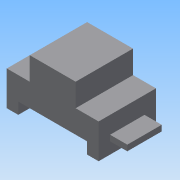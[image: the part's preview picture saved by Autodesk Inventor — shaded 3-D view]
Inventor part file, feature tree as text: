
AUTODESK INVENTOR PART (.ipt)
format: ipt  version: 2015 (Build 190159000, 159)  size: 96,768 bytes
history: native  units: in
note: dims shown in document units (in); Inventor stores cm internally (conversion verified against a paired STEP export)
features: sketch x4, extrude x2
ambient origin geometry x8: Origin, YZ Plane, XZ Plane, XY Plane, X Axis, Y Axis, Z Axis, Center Point
bodies: Solid1 (feature_tree)
feature tree (6):
  extrude  "Extrusion1"  Depth=1.0in
  sketch  "Sketch2"  dims[d2=1.0in d3=2.0in]
  sketch  "Sketch3"  dims[d4=1.0in]
  extrude  "Extrusion2"  Depth=2.0in
  sketch  "Sketch1"  dims[d0=1.5in d1=1.0in]
  sketch  "Sketch4"  dims[d5=1.5in d6=0.5in d7=0.5in d8=3.0in d9=2.5in d10=0.0in d11=1.5in d12=0.25in d13=0.5in d14=0.75in d15=0.0in]
